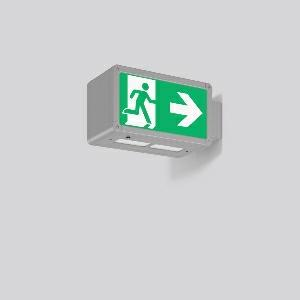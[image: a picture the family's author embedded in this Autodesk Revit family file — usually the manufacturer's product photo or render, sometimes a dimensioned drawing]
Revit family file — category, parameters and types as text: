
# Revit family: rechteck_wandausleger_671049_004_04_6d29
name_source: partatom
category: Lighting Fixtures
units: mm (PartAtom-declared; Revit-internal decimal feet)

## family parameters
Cut with Voids When Loaded = No
Host = Face
Light Source = No
Part Type = Normal
Room Calculation Point = No
Round Connector Dimension = Use Diameter
Shared = No

## types (1)
- RECHTECK wandausleger
    Apparent Load = 0 VA
    Default Elevation = 1800 mm
    Description = Series: RECHTECK
Rectangular wall extension luminaire in classic design. For escape route identification. Housing: aluminium, with plastic corner connectors. Display panels: plastic, opal, with motifs on one side/on both sides. Wall extension Electronic ballast included. Self-contained system with automatic self-test and feedback to the RZB monitoring system MULTIDIGIT. Please indicate legend number when placing your order! 
Colour: anodised aluminium
Length: 250 mm
Width: 125 mm
Height: 140 mm
Weight: 1.5 kg
Operating mode: maintained power mode
Viewing Distance: 21 m
Duration time: 3 h
Lamp: LED
Socket: without socket
Colour temperature: 6500K
Colour rendering index (CRI): 70
System power: 6.9 W
Control gear: Regulated power supply
Protection class: I
Type of protection: IP 44
    Height = 140 mm  [stored 0.459318 ft]
    Lamp = 0 x
    Length = 250 mm
    Luminous efficacy = 0 lm/W
    Manufacturer = RZB
    ModVariant = No
    Model = 671049.004.04
    Mounting Place = Wall
    Mounting Type = Surface mounted
    Number of Poles = 1
    OnlyDefault = Yes
    Power Factor = 1
    Product Name = RECHTECK wandausleger
    Product group = wall cantilever luminaires
    ProductGroupID = 2005
    Protection Class = Protection class I
    Protection Degree = IP 44
    RLX_Detail_Level = 1
    RLX_Emergency_Light_Flux = 0 lm
    RLX_Emergency_Type = 0
    RLX_Emergency_Type_DB = No
    RlxData = <blob elided: 22689 chars, md5=4e6797de>
    Standby Power = 0 W
    System Light Flux = 0 lm
    System Power = 0 W
    Type Comments = Product without accessories
    Type Image = 671049.004.jpg
    URL = http://relux.com
    VarID = ---
    Voltage = 230 V
    Voltage Range = 220-240 V
    Weight = 0.00 kg
    Width = 125 mm

note: [stored X ft] marks values corroborated as IEEE doubles in the binary element streams (Revit-internal decimal feet)

## geometry (parser evidence)
native form markers: Blend x4, Sweep x10
no freeform markers — native parametric forms only
